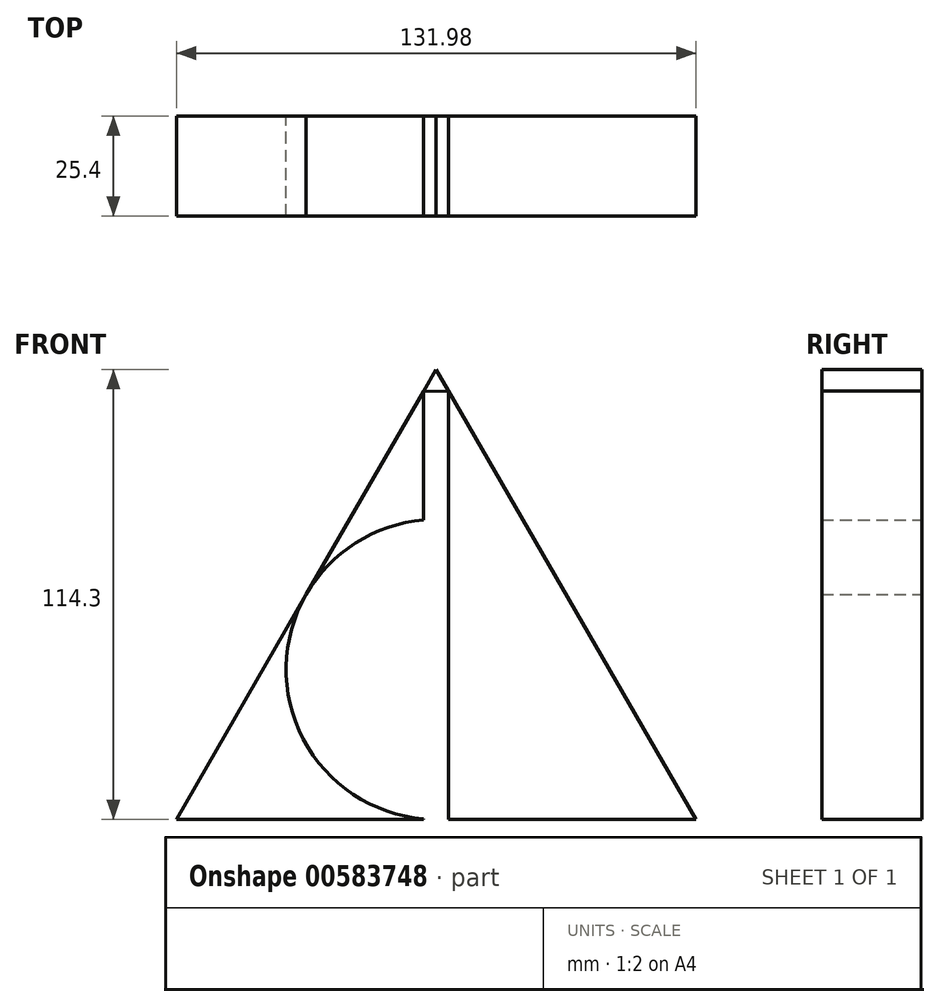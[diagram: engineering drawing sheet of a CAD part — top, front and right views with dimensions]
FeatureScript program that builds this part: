
annotation { "Feature Type Name" : "Feature", "Feature Type Description" : "" }
export const myFeature = defineFeature(function(context is Context, id is Id, definition is map)
    precondition{}
    {
        {
            var Q0;
            Q0=qCreatedBy(makeId("Front.planeOp"),FACE);
            var sketch = newSketch(context, id + "F0", { "sketchPlane" : qUnion([Q0])});
            skCircle(sketch, "E0", {"center": v(0, 0) * mm, "radius": 38.1 * mm});
            skCircle(sketch, "E1.cCircle", {"center": v(0, 0) * mm, "radius": 38.1 * mm, "construction": true});
            skLineSegment(sketch, "E2.0", {"start": v(66, -38.1) * mm, "end": v(-66, -38.1) * mm});
            skLineSegment(sketch, "E2.1", {"start": v(-66, -38.1) * mm, "end": v(0, 76.2) * mm});
            skLineSegment(sketch, "E2.2", {"start": v(0, 76.2) * mm, "end": v(66, -38.1) * mm});
            skPoint(sketch, "E2.0.midPoint", {"position": v(0, -38.1) * mm});
            skLineSegment(sketch, "E3", {"start": v(-3.2, 70.67) * mm, "end": v(-3.2, -38.1) * mm});
            skLineSegment(sketch, "E4", {"start": v(-3.2, -38.1) * mm, "end": v(3.16, -38.1) * mm});
            skLineSegment(sketch, "E5", {"start": v(3.16, -38.1) * mm, "end": v(3.16, 70.73) * mm});
            skLineSegment(sketch, "E6", {"start": v(-3.2, 70.67) * mm, "end": v(3.16, 70.73) * mm});
            skSolve(sketch);
        }
        {
            var Q0;
            {var subQ3=sQuery(id+"F0.wireOp",EDGE,"E6");Q0=makeQuery(id+"F0.imprint","IMPRINT",FACE,{"disambiguationData":[TD([[makeQuery(id+"F0.imprint","IMPRINT",EDGE,{"derivedFrom":subQ3}),1.0]])]});}
            var Q1;
            {var subQ0=sQuery(id+"F0.wireOp",EDGE,"E2.1");var subQ1=sQuery(id+"F0.wireOp",EDGE,"E0");var subQ2=makeQuery(id+"F0.imprint","INTERSECT",VERTEX,{"derivedFrom":[subQ1,subQ0]});Q1=makeQuery(id+"F0.imprint","IMPRINT",FACE,{"disambiguationData":[TD([[makeQuery(id+"F0.imprint","IMPRINT",EDGE,{"disambiguationData":[TD([[subQ2,1.0]])],"derivedFrom":subQ1}),-1.0]])]});}
            var Q2;
            {var subQ0=sQuery(id+"F0.wireOp",EDGE,"E2.2");var subQ1=sQuery(id+"F0.wireOp",EDGE,"E0");var subQ2=makeQuery(id+"F0.imprint","INTERSECT",VERTEX,{"derivedFrom":[subQ1,subQ0]});Q2=makeQuery(id+"F0.imprint","IMPRINT",FACE,{"disambiguationData":[TD([[makeQuery(id+"F0.imprint","IMPRINT",EDGE,{"disambiguationData":[TD([[subQ2,-1.0]])],"derivedFrom":subQ1}),-1.0]])]});}
            var Q3;
            {var subQ0=sQuery(id+"F0.wireOp",EDGE,"E0");var subQ2=sQuery(id+"F0.wireOp",EDGE,"E5");var subQ7=makeQuery(id+"F0.imprint","INTERSECT",VERTEX,{"disambiguationData":[OD(0.0)],"derivedFrom":[subQ0,subQ2]});Q3=makeQuery(id+"F0.imprint","IMPRINT",FACE,{"disambiguationData":[TD([[makeQuery(id+"F0.imprint","IMPRINT",EDGE,{"disambiguationData":[TD([[subQ7,-1.0]])],"derivedFrom":subQ0}),1.0]])]});}
            var Q4;
            {var subQ0=sQuery(id+"F0.wireOp",EDGE,"E2.1");var subQ1=sQuery(id+"F0.wireOp",EDGE,"E0");var subQ2=makeQuery(id+"F0.imprint","INTERSECT",VERTEX,{"derivedFrom":[subQ1,subQ0]});Q4=makeQuery(id+"F0.imprint","IMPRINT",FACE,{"disambiguationData":[TD([[makeQuery(id+"F0.imprint","IMPRINT",EDGE,{"disambiguationData":[TD([[subQ2,-1.0]])],"derivedFrom":subQ1}),-1.0]])]});}
            var Q5;
            {var subQ0=sQuery(id+"F0.wireOp",EDGE,"E2.2");var subQ1=sQuery(id+"F0.wireOp",EDGE,"E0");var subQ2=makeQuery(id+"F0.imprint","INTERSECT",VERTEX,{"derivedFrom":[subQ1,subQ0]});Q5=makeQuery(id+"F0.imprint","IMPRINT",FACE,{"disambiguationData":[TD([[makeQuery(id+"F0.imprint","IMPRINT",EDGE,{"disambiguationData":[TD([[subQ2,1.0]])],"derivedFrom":subQ1}),-1.0]])]});}
            extrude(context, id + "F1", {"entities" : qUnion([Q0, Q1, Q2, Q3, Q4, Q5]), "depth" : 25.4 * mm, "offsetDistance" : 25.4 * mm});
        }
    });
